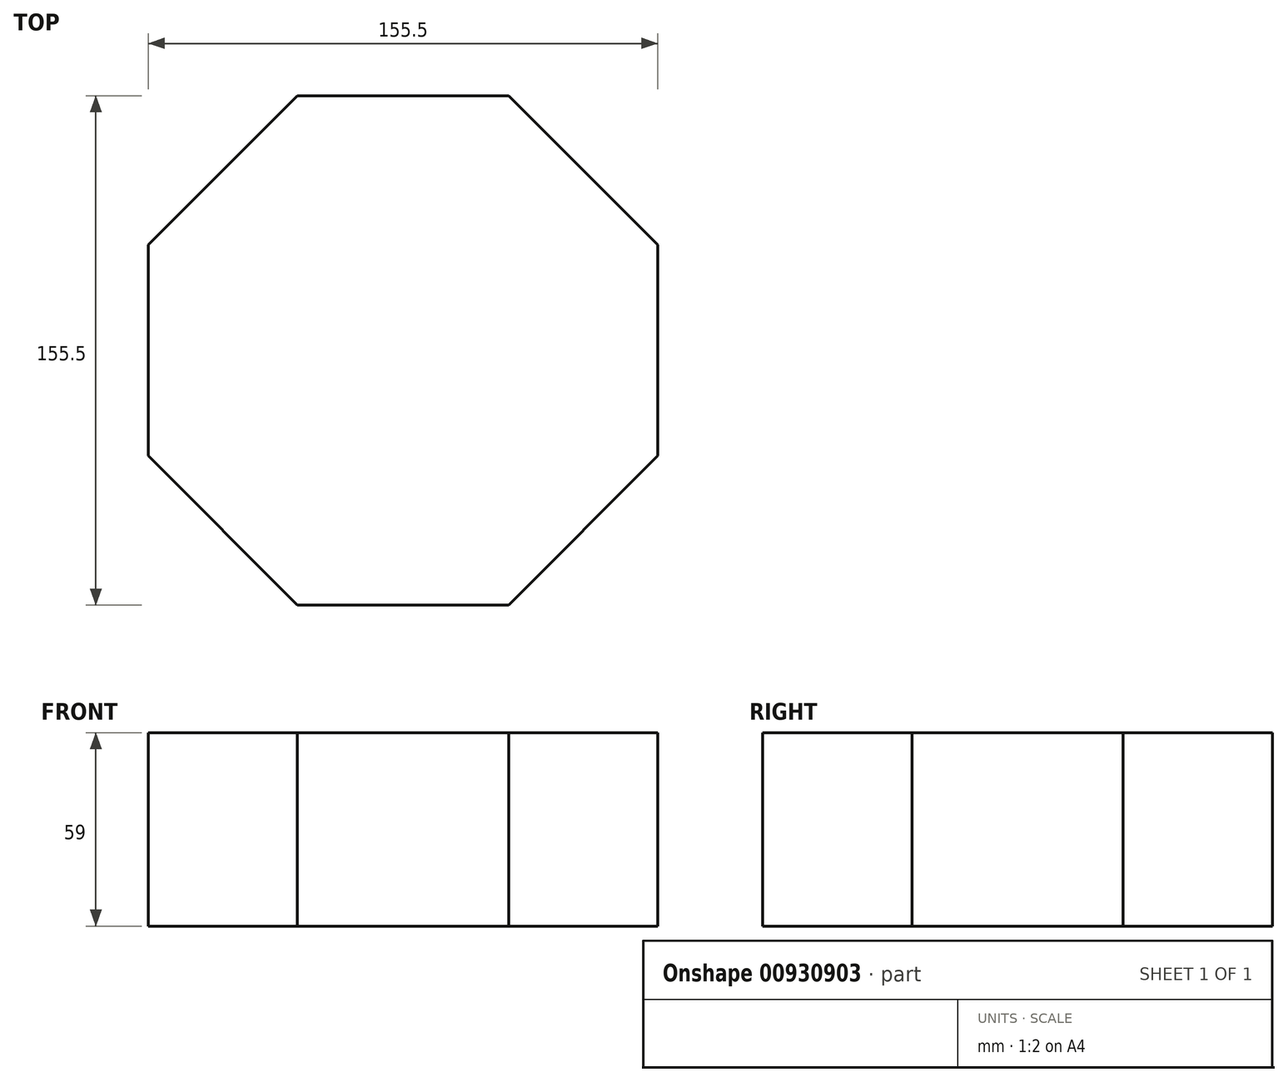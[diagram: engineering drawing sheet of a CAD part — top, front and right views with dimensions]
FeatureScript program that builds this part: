
annotation { "Feature Type Name" : "Feature", "Feature Type Description" : "" }
export const myFeature = defineFeature(function(context is Context, id is Id, definition is map)
    precondition{}
    {
        {
            var Q0;
            Q0=qCreatedBy(makeId("Top.planeOp"),FACE);
            var sketch = newSketch(context, id + "F0", { "sketchPlane" : qUnion([Q0])});
            skCircle(sketch, "E0.cCircle", {"center": v(0, 0) * mm, "radius": 77.75 * mm, "construction": true});
            skLineSegment(sketch, "E0.0", {"start": v(-32.2, 77.75) * mm, "end": v(32.2, 77.75) * mm});
            skLineSegment(sketch, "E0.1", {"start": v(32.2, 77.75) * mm, "end": v(77.75, 32.2) * mm});
            skLineSegment(sketch, "E0.2", {"start": v(77.75, 32.2) * mm, "end": v(77.75, -32.2) * mm});
            skLineSegment(sketch, "E0.3", {"start": v(77.75, -32.2) * mm, "end": v(32.2, -77.75) * mm});
            skLineSegment(sketch, "E0.4", {"start": v(32.2, -77.75) * mm, "end": v(-32.2, -77.75) * mm});
            skLineSegment(sketch, "E0.5", {"start": v(-32.2, -77.75) * mm, "end": v(-77.75, -32.2) * mm});
            skLineSegment(sketch, "E0.6", {"start": v(-77.75, -32.2) * mm, "end": v(-77.75, 32.2) * mm});
            skLineSegment(sketch, "E0.7", {"start": v(-77.75, 32.2) * mm, "end": v(-32.2, 77.75) * mm});
            skPoint(sketch, "E0.0.midPoint", {"position": v(0, 77.75) * mm});
            skLineSegment(sketch, "E1.0", {"start": v(-73.25, 30.34) * mm, "end": v(-30.34, 73.25) * mm, "construction": true});
            skLineSegment(sketch, "E1.1", {"start": v(-73.25, -30.34) * mm, "end": v(-73.25, 30.34) * mm, "construction": true});
            skLineSegment(sketch, "E1.2", {"start": v(-30.34, 73.25) * mm, "end": v(30.34, 73.25) * mm, "construction": true});
            skLineSegment(sketch, "E1.3", {"start": v(-30.34, -73.25) * mm, "end": v(-73.25, -30.34) * mm, "construction": true});
            skLineSegment(sketch, "E1.4", {"start": v(30.34, 73.25) * mm, "end": v(73.25, 30.34) * mm, "construction": true});
            skLineSegment(sketch, "E1.5", {"start": v(73.25, 30.34) * mm, "end": v(73.25, -30.34) * mm, "construction": true});
            skLineSegment(sketch, "E1.6", {"start": v(73.25, -30.34) * mm, "end": v(30.34, -73.25) * mm, "construction": true});
            skLineSegment(sketch, "E1.7", {"start": v(30.34, -73.25) * mm, "end": v(-30.34, -73.25) * mm, "construction": true});
            skLineSegment(sketch, "E2", {"start": v(-77.75, 0) * mm, "end": v(-65.25, 0) * mm, "construction": true});
            skPoint(sketch, "E2.endSnap0", {"position": v(77.75, 0) * mm});
            skLineSegment(sketch, "E3", {"start": v(77.75, 0) * mm, "end": v(61.45, 0) * mm, "construction": true});
            skCircle(sketch, "E4", {"center": v(-65.25, 0) * mm, "radius": 2 * mm, "construction": true});
            skArc(sketch, "E5", {"start": v(61.45, -2) * mm, "mid": v(63.45, 0) * mm, "end": v(61.45, 2) * mm, "construction": true});
            skArc(sketch, "E6", {"start": v(59.45, 2) * mm, "mid": v(57.45, 0) * mm, "end": v(59.45, -2) * mm, "construction": true});
            skLineSegment(sketch, "E7", {"start": v(59.45, 2) * mm, "end": v(61.45, 2) * mm, "construction": true});
            skLineSegment(sketch, "E8.MirrorCS", {"start": v(59.45, -2) * mm, "end": v(61.45, -2) * mm, "construction": true});
            skSolve(sketch);
        }
        {
            var Q0;
            Q0 = qSketchRegion(id + "F0", true);
            extrude(context, id + "F1", {"entities" : qUnion([Q0]), "depth" : 59 * mm, "offsetDistance" : 25 * mm});
        }
    });
